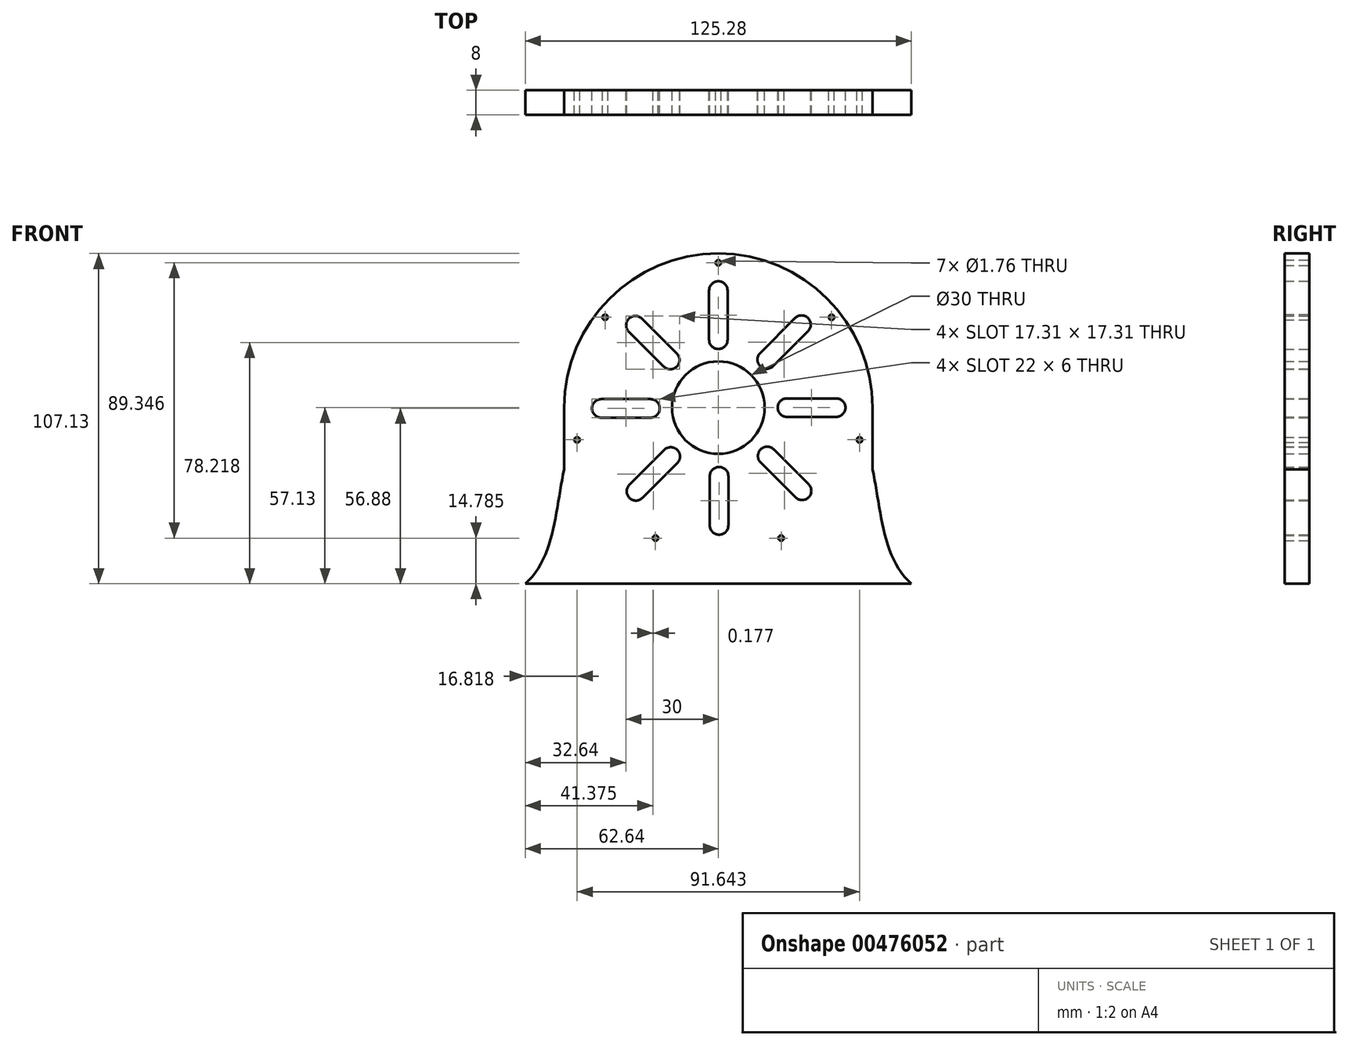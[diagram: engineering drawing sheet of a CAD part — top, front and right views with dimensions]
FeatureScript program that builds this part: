
annotation { "Feature Type Name" : "Feature", "Feature Type Description" : "" }
export const myFeature = defineFeature(function(context is Context, id is Id, definition is map)
    precondition{}
    {
        {
            var Q0;
            Q0=qCreatedBy(makeId("Front.planeOp"),FACE);
            var sketch = newSketch(context, id + "F0", { "sketchPlane" : qUnion([Q0])});
            skArc(sketch, "E0", {"start": v(50, 0) * mm, "mid": v(0, 50) * mm, "end": v(-50, 0) * mm});
            skLineSegment(sketch, "E1", {"start": v(-50, 0) * mm, "end": v(-50, -20) * mm});
            skLineSegment(sketch, "E2", {"start": v(-62.64, -57.13) * mm, "end": v(0, -57.13) * mm});
            skLineSegment(sketch, "E3.MirrorCS", {"start": v(62.64, -57.13) * mm, "end": v(0, -57.13) * mm});
            skLineSegment(sketch, "E4.MirrorCS", {"start": v(50, 0) * mm, "end": v(50, -20) * mm});
            skFitSpline(sketch, "E5", {"points": [v(-50, -20) * mm, v(-62.64, -57.13) * mm], "startDerivative": vector(-8.6, -38.71) * mm, "endDerivative": vector(-28.77, -25) * mm});
            skFitSpline(sketch, "E6.MirrorCS", {"points": [v(50, -20) * mm, v(62.64, -57.13) * mm], "startDerivative": vector(8.6, -38.71) * mm, "endDerivative": vector(28.77, -25) * mm});
            skCircle(sketch, "E7", {"center": v(0, 0) * mm, "radius": 15 * mm});
            skArc(sketch, "E8", {"start": v(3, 38) * mm, "mid": v(0, 41) * mm, "end": v(-3, 38) * mm});
            skArc(sketch, "E9", {"start": v(-3, 22) * mm, "mid": v(0, 19) * mm, "end": v(3, 22) * mm});
            skLineSegment(sketch, "E10", {"start": v(-3, 38) * mm, "end": v(-3, 22) * mm});
            skLineSegment(sketch, "E11", {"start": v(3, 38) * mm, "end": v(3, 22) * mm});
            skLineSegment(sketch, "E12.1.0", {"start": v(-24.8, 28.87) * mm, "end": v(-13.49, 17.55) * mm});
            skArc(sketch, "E12.1.1", {"start": v(-24.8, 28.87) * mm, "mid": v(-29.04, 28.87) * mm, "end": v(-29.04, 24.62) * mm});
            skLineSegment(sketch, "E12.1.2", {"start": v(-29.04, 24.62) * mm, "end": v(-17.73, 13.31) * mm});
            skArc(sketch, "E12.1.3", {"start": v(-17.73, 13.31) * mm, "mid": v(-13.49, 13.31) * mm, "end": v(-13.49, 17.55) * mm});
            skLineSegment(sketch, "E12.2.0", {"start": v(-38, 2.75) * mm, "end": v(-22, 2.75) * mm});
            skArc(sketch, "E12.2.1", {"start": v(-38, 2.75) * mm, "mid": v(-41, -0.25) * mm, "end": v(-38, -3.25) * mm});
            skLineSegment(sketch, "E12.2.2", {"start": v(-38, -3.25) * mm, "end": v(-22, -3.25) * mm});
            skArc(sketch, "E12.2.3", {"start": v(-22, -3.25) * mm, "mid": v(-19, -0.25) * mm, "end": v(-22, 2.75) * mm});
            skLineSegment(sketch, "E12.3.0", {"start": v(-28.87, -25.05) * mm, "end": v(-17.55, -13.74) * mm});
            skArc(sketch, "E12.3.1", {"start": v(-28.87, -25.05) * mm, "mid": v(-28.87, -29.3) * mm, "end": v(-24.62, -29.3) * mm});
            skLineSegment(sketch, "E12.3.2", {"start": v(-24.62, -29.3) * mm, "end": v(-13.31, -17.98) * mm});
            skArc(sketch, "E12.3.3", {"start": v(-13.31, -17.98) * mm, "mid": v(-13.31, -13.74) * mm, "end": v(-17.55, -13.74) * mm});
            skLineSegment(sketch, "E12.4.0", {"start": v(-2.75, -38.25) * mm, "end": v(-2.75, -22.25) * mm});
            skArc(sketch, "E12.4.1", {"start": v(-2.75, -38.25) * mm, "mid": v(0.25, -41.25) * mm, "end": v(3.25, -38.25) * mm});
            skLineSegment(sketch, "E12.4.2", {"start": v(3.25, -38.25) * mm, "end": v(3.25, -22.25) * mm});
            skArc(sketch, "E12.4.3", {"start": v(3.25, -22.25) * mm, "mid": v(0.25, -19.25) * mm, "end": v(-2.75, -22.25) * mm});
            skLineSegment(sketch, "E12.5.0", {"start": v(25.05, -29.12) * mm, "end": v(13.74, -17.8) * mm});
            skArc(sketch, "E12.5.1", {"start": v(25.05, -29.12) * mm, "mid": v(29.3, -29.12) * mm, "end": v(29.3, -24.87) * mm});
            skLineSegment(sketch, "E12.5.2", {"start": v(29.3, -24.87) * mm, "end": v(17.98, -13.56) * mm});
            skArc(sketch, "E12.5.3", {"start": v(17.98, -13.56) * mm, "mid": v(13.74, -13.56) * mm, "end": v(13.74, -17.8) * mm});
            skLineSegment(sketch, "E12.6.0", {"start": v(38.25, -3) * mm, "end": v(22.25, -3) * mm});
            skArc(sketch, "E12.6.1", {"start": v(38.25, -3) * mm, "mid": v(41.25, 0) * mm, "end": v(38.25, 3) * mm});
            skLineSegment(sketch, "E12.6.2", {"start": v(38.25, 3) * mm, "end": v(22.25, 3) * mm});
            skArc(sketch, "E12.6.3", {"start": v(22.25, 3) * mm, "mid": v(19.25, 0) * mm, "end": v(22.25, -3) * mm});
            skLineSegment(sketch, "E12.7.0", {"start": v(29.12, 24.8) * mm, "end": v(17.8, 13.49) * mm});
            skArc(sketch, "E12.7.1", {"start": v(29.12, 24.8) * mm, "mid": v(29.12, 29.04) * mm, "end": v(24.87, 29.04) * mm});
            skLineSegment(sketch, "E12.7.2", {"start": v(24.87, 29.04) * mm, "end": v(13.56, 17.73) * mm});
            skArc(sketch, "E12.7.3", {"start": v(13.56, 17.73) * mm, "mid": v(13.56, 13.49) * mm, "end": v(17.8, 13.49) * mm});
            skPoint(sketch, "E12.center", {"position": v(0.12, -0.12) * mm});
            skCircle(sketch, "E13", {"center": v(0, 0) * mm, "radius": 44 * mm, "construction": true});
            skCircle(sketch, "E14", {"center": v(0, 47) * mm, "radius": 0.88 * mm});
            skPoint(sketch, "E14.centerSnap0", {"position": v(0, 50) * mm});
            skCircle(sketch, "E15.1.0", {"center": v(-36.75, 29.3) * mm, "radius": 0.88 * mm});
            skCircle(sketch, "E15.2.0", {"center": v(-45.82, -10.46) * mm, "radius": 0.88 * mm});
            skCircle(sketch, "E15.3.0", {"center": v(-20.4, -42.35) * mm, "radius": 0.88 * mm});
            skCircle(sketch, "E15.4.0", {"center": v(20.4, -42.35) * mm, "radius": 0.88 * mm});
            skCircle(sketch, "E15.5.0", {"center": v(45.82, -10.46) * mm, "radius": 0.88 * mm});
            skCircle(sketch, "E15.6.0", {"center": v(36.75, 29.3) * mm, "radius": 0.88 * mm});
            skSolve(sketch);
        }
        {
            var Q0;
            Q0 = qSketchRegion(id + "F0", true);
            extrude(context, id + "F1", {"entities" : qUnion([Q0]), "depth" : 8 * mm});
        }
    });
